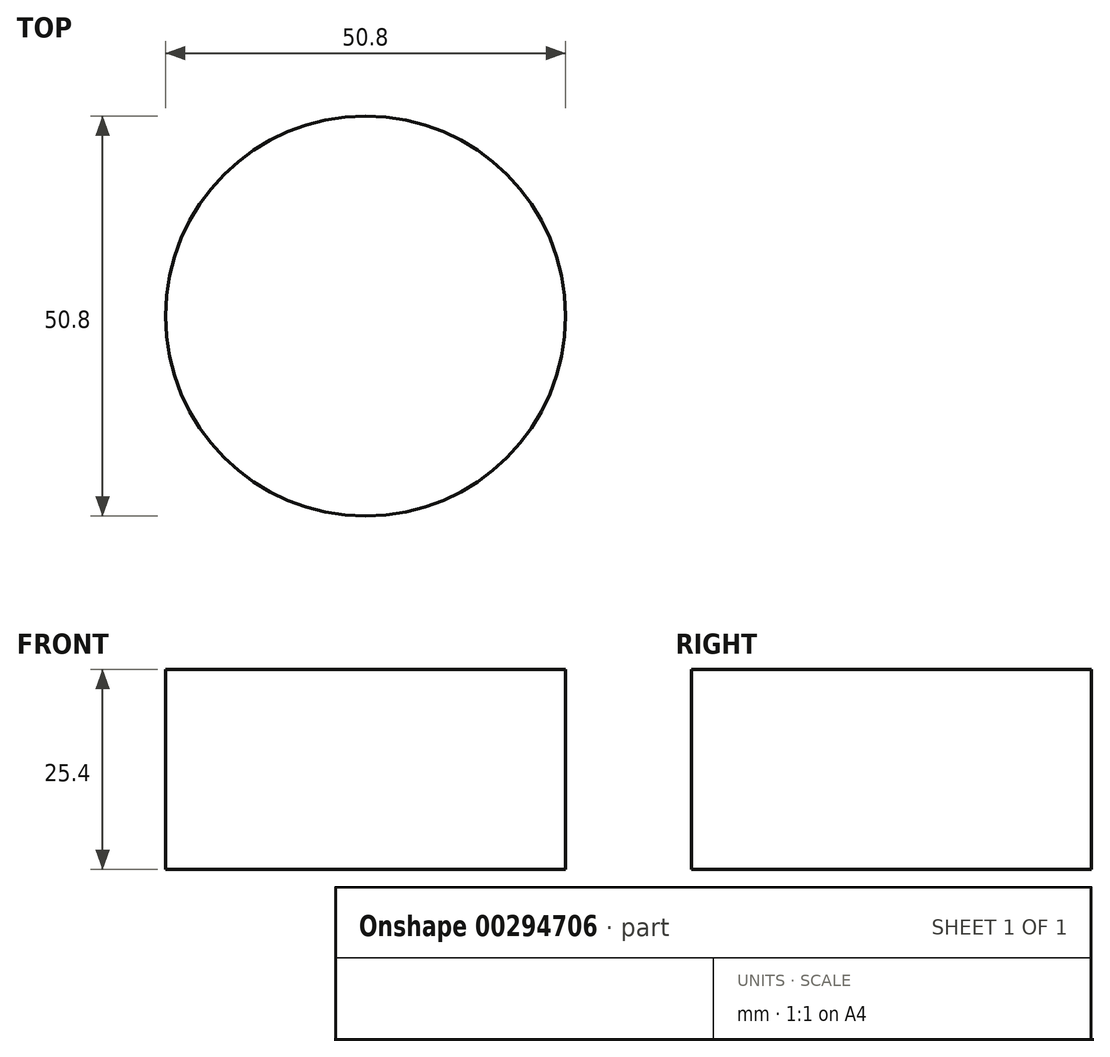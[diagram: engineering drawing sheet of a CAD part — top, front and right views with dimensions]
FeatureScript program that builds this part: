
annotation { "Feature Type Name" : "Feature", "Feature Type Description" : "" }
export const myFeature = defineFeature(function(context is Context, id is Id, definition is map)
    precondition{}
    {
        {
            var Q0;
            Q0=qCreatedBy(makeId("Top.planeOp"),FACE);
            var sketch = newSketch(context, id + "F0", { "sketchPlane" : qUnion([Q0])});
            skCircle(sketch, "E0", {"center": v(0, 0) * mm, "radius": 25.4 * mm});
            skSolve(sketch);
        }
        {
            var Q0;
            Q0 = qSketchRegion(id + "F0", true);
            extrude(context, id + "F1", {"entities" : qUnion([Q0]), "depth" : 25.4 * mm});
        }
    });
